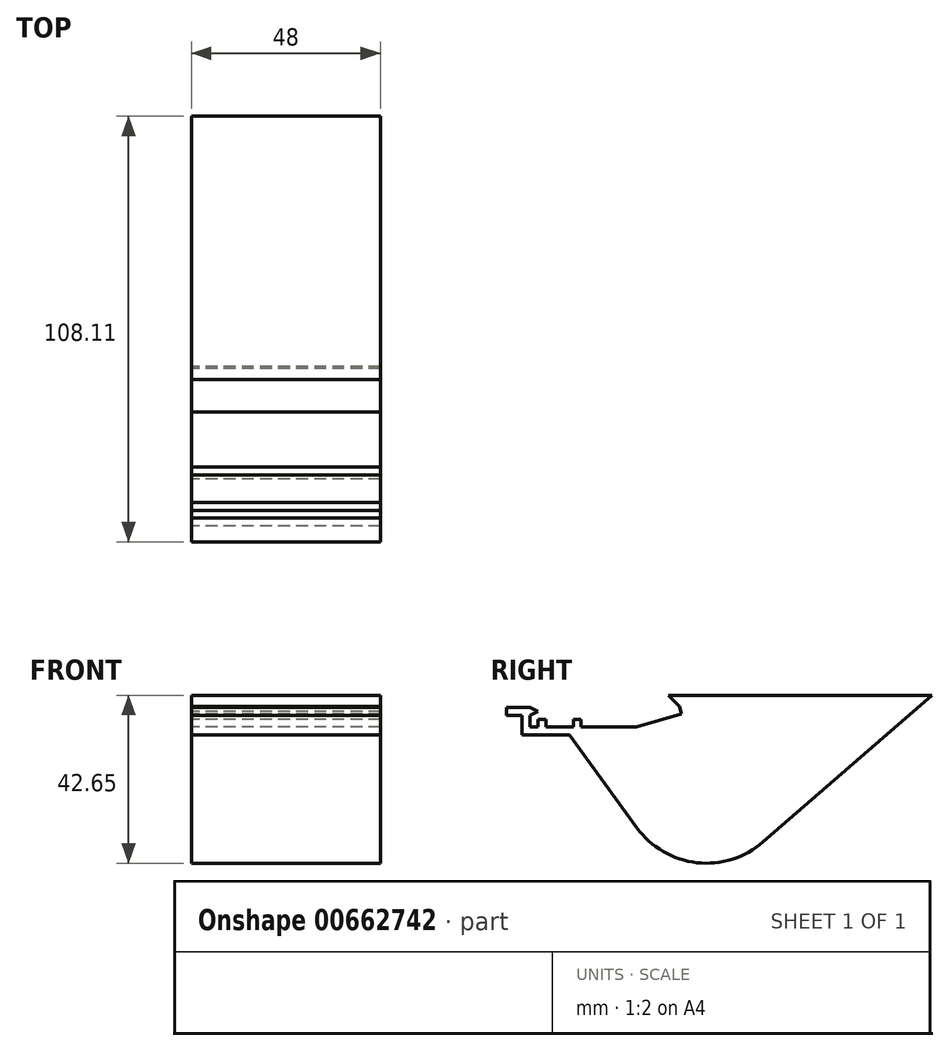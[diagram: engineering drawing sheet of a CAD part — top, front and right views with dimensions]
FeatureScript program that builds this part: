
annotation { "Feature Type Name" : "Feature", "Feature Type Description" : "" }
export const myFeature = defineFeature(function(context is Context, id is Id, definition is map)
    precondition{}
    {
        {
            var Q0;
            Q0=qCreatedBy(makeId("Right.planeOp"),FACE);
            var sketch = newSketch(context, id + "F0", { "sketchPlane" : qUnion([Q0])});
            skLineSegment(sketch, "E0", {"start": v(-13.84, 26.27) * mm, "end": v(53.08, 26.27) * mm});
            skLineSegment(sketch, "E1", {"start": v(53.08, 26.27) * mm, "end": v(10.2, -11) * mm});
            skLineSegment(sketch, "E2", {"start": v(-21.93, -7.35) * mm, "end": v(-39.03, 16.2) * mm});
            skLineSegment(sketch, "E3", {"start": v(-51.03, 16.2) * mm, "end": v(-51.03, 23.2) * mm});
            skLineSegment(sketch, "E4", {"start": v(-51.03, 23.2) * mm, "end": v(-49.03, 23.2) * mm});
            skLineSegment(sketch, "E5", {"start": v(-49.03, 23.2) * mm, "end": v(-49.03, 18.2) * mm});
            skPoint(sketch, "E6", {"position": v(-10.5, 21.5) * mm});
            skLineSegment(sketch, "E7", {"start": v(-22.03, 18.2) * mm, "end": v(-10.5, 21.5) * mm});
            skLineSegment(sketch, "E8", {"start": v(-49.03, 18.2) * mm, "end": v(-22.03, 18.2) * mm});
            skLineSegment(sketch, "E9", {"start": v(-49.03, 18.2) * mm, "end": v(-49.03, 16.2) * mm});
            skLineSegment(sketch, "E10", {"start": v(-51.03, 16.2) * mm, "end": v(-49.03, 16.2) * mm});
            skLineSegment(sketch, "E11", {"start": v(-39.03, 16.2) * mm, "end": v(-49.03, 16.2) * mm});
            skLineSegment(sketch, "E12", {"start": v(-49.03, 23.2) * mm, "end": v(-47.03, 22.2) * mm});
            skLineSegment(sketch, "E13", {"start": v(-47.03, 22.2) * mm, "end": v(-49.03, 21.2) * mm});
            skLineSegment(sketch, "E14", {"start": v(-49.03, 21.2) * mm, "end": v(-49.03, 22.2) * mm});
            skLineSegment(sketch, "E15", {"start": v(-49.03, 22.2) * mm, "end": v(-47.03, 22.2) * mm});
            skLineSegment(sketch, "E16", {"start": v(-13.84, 26.27) * mm, "end": v(-11.04, 23.42) * mm});
            skLineSegment(sketch, "E17", {"start": v(-11.04, 23.42) * mm, "end": v(-10.5, 21.5) * mm});
            skLineSegment(sketch, "E18.bottom", {"start": v(-47.03, 20.2) * mm, "end": v(-45.03, 20.2) * mm});
            skLineSegment(sketch, "E18.top", {"start": v(-47.03, 18.2) * mm, "end": v(-45.03, 18.2) * mm});
            skLineSegment(sketch, "E18.left", {"start": v(-47.03, 20.2) * mm, "end": v(-47.03, 18.2) * mm});
            skLineSegment(sketch, "E18.right", {"start": v(-45.03, 20.2) * mm, "end": v(-45.03, 18.2) * mm});
            skLineSegment(sketch, "E19.bottom", {"start": v(-38.03, 20.2) * mm, "end": v(-36.03, 20.2) * mm});
            skLineSegment(sketch, "E19.top", {"start": v(-38.03, 18.2) * mm, "end": v(-36.03, 18.2) * mm});
            skLineSegment(sketch, "E19.left", {"start": v(-38.03, 20.2) * mm, "end": v(-38.03, 18.2) * mm});
            skLineSegment(sketch, "E19.right", {"start": v(-36.03, 20.2) * mm, "end": v(-36.03, 18.2) * mm});
            skLineSegment(sketch, "E20.bottom", {"start": v(-51.03, 23.2) * mm, "end": v(-55.03, 23.2) * mm});
            skLineSegment(sketch, "E20.top", {"start": v(-51.03, 21.2) * mm, "end": v(-55.03, 21.2) * mm});
            skLineSegment(sketch, "E20.left", {"start": v(-51.03, 23.2) * mm, "end": v(-51.03, 21.2) * mm});
            skLineSegment(sketch, "E20.right", {"start": v(-55.03, 23.2) * mm, "end": v(-55.03, 21.2) * mm});
            skLineSegment(sketch, "E21.bottom", {"start": v(-36.03, 18.2) * mm, "end": v(-34.03, 18.2) * mm});
            skLineSegment(sketch, "E21.top", {"start": v(-36.03, 22.2) * mm, "end": v(-34.03, 22.2) * mm});
            skLineSegment(sketch, "E21.left", {"start": v(-36.03, 18.2) * mm, "end": v(-36.03, 22.2) * mm});
            skLineSegment(sketch, "E21.right", {"start": v(-34.03, 18.2) * mm, "end": v(-34.03, 22.2) * mm});
            skLineSegment(sketch, "E22", {"start": v(14.5, -7.26) * mm, "end": v(-10.5, 21.5) * mm});
            skArc(sketch, "E23", {"start": v(-21.93, -7.35) * mm, "mid": v(-6.67, -16.24) * mm, "end": v(10.2, -11) * mm});
            skSolve(sketch);
        }
        {
            var Q0;
            Q0=makeQuery(id+"F0.imprint","IMPRINT",FACE,{"disambiguationData":[TD([[makeQuery(id+"F0.imprint","IMPRINT",EDGE,{"derivedFrom":sQuery(id+"F0.wireOp",EDGE,"E2")}),-1.0]])]});
            var Q1;
            {var subQ1=sQuery(id+"F0.wireOp",EDGE,"E0");Q1=makeQuery(id+"F0.imprint","IMPRINT",FACE,{"disambiguationData":[TD([[makeQuery(id+"F0.imprint","IMPRINT",EDGE,{"derivedFrom":subQ1}),-1.0]])]});}
            var Q2;
            {var subQ3=sQuery(id+"F0.wireOp",EDGE,"E21.bottom");Q2=makeQuery(id+"F0.imprint","IMPRINT",FACE,{"disambiguationData":[TD([[makeQuery(id+"F0.imprint","IMPRINT",EDGE,{"derivedFrom":subQ3}),1.0]])]});}
            var Q3;
            {var subQ0=sQuery(id+"F0.wireOp",EDGE,"E19.bottom");Q3=makeQuery(id+"F0.imprint","IMPRINT",FACE,{"disambiguationData":[TD([[makeQuery(id+"F0.imprint","IMPRINT",EDGE,{"derivedFrom":subQ0}),-1.0]])]});}
            var Q4;
            Q4=makeQuery(id+"F0.imprint","IMPRINT",FACE,{"disambiguationData":[TD([[makeQuery(id+"F0.imprint","IMPRINT",EDGE,{"derivedFrom":sQuery(id+"F0.wireOp",EDGE,"E18.bottom")}),-1.0]])]});
            var Q5;
            Q5=makeQuery(id+"F0.imprint","IMPRINT",FACE,{"disambiguationData":[TD([[makeQuery(id+"F0.imprint","IMPRINT",EDGE,{"derivedFrom":sQuery(id+"F0.wireOp",EDGE,"E3")}),-1.0]])]});
            var Q6;
            Q6=makeQuery(id+"F0.imprint","IMPRINT",FACE,{"disambiguationData":[TD([[makeQuery(id+"F0.imprint","IMPRINT",EDGE,{"derivedFrom":sQuery(id+"F0.wireOp",EDGE,"E13")}),-1.0]])]});
            var Q7;
            {var subQ0=sQuery(id+"F0.wireOp",EDGE,"E12");Q7=makeQuery(id+"F0.imprint","IMPRINT",FACE,{"disambiguationData":[TD([[makeQuery(id+"F0.imprint","IMPRINT",EDGE,{"derivedFrom":subQ0}),-1.0]])]});}
            var Q8;
            Q8=makeQuery(id+"F0.imprint","IMPRINT",FACE,{"disambiguationData":[TD([[makeQuery(id+"F0.imprint","IMPRINT",EDGE,{"derivedFrom":sQuery(id+"F0.wireOp",EDGE,"E20.bottom")}),1.0]])]});
            extrude(context, id + "F1", {"entities" : qUnion([Q0, Q1, Q2, Q3, Q4, Q5, Q6, Q7, Q8]), "depth" : 48 * mm, "offsetDistance" : 25.4 * mm});
        }
    });
